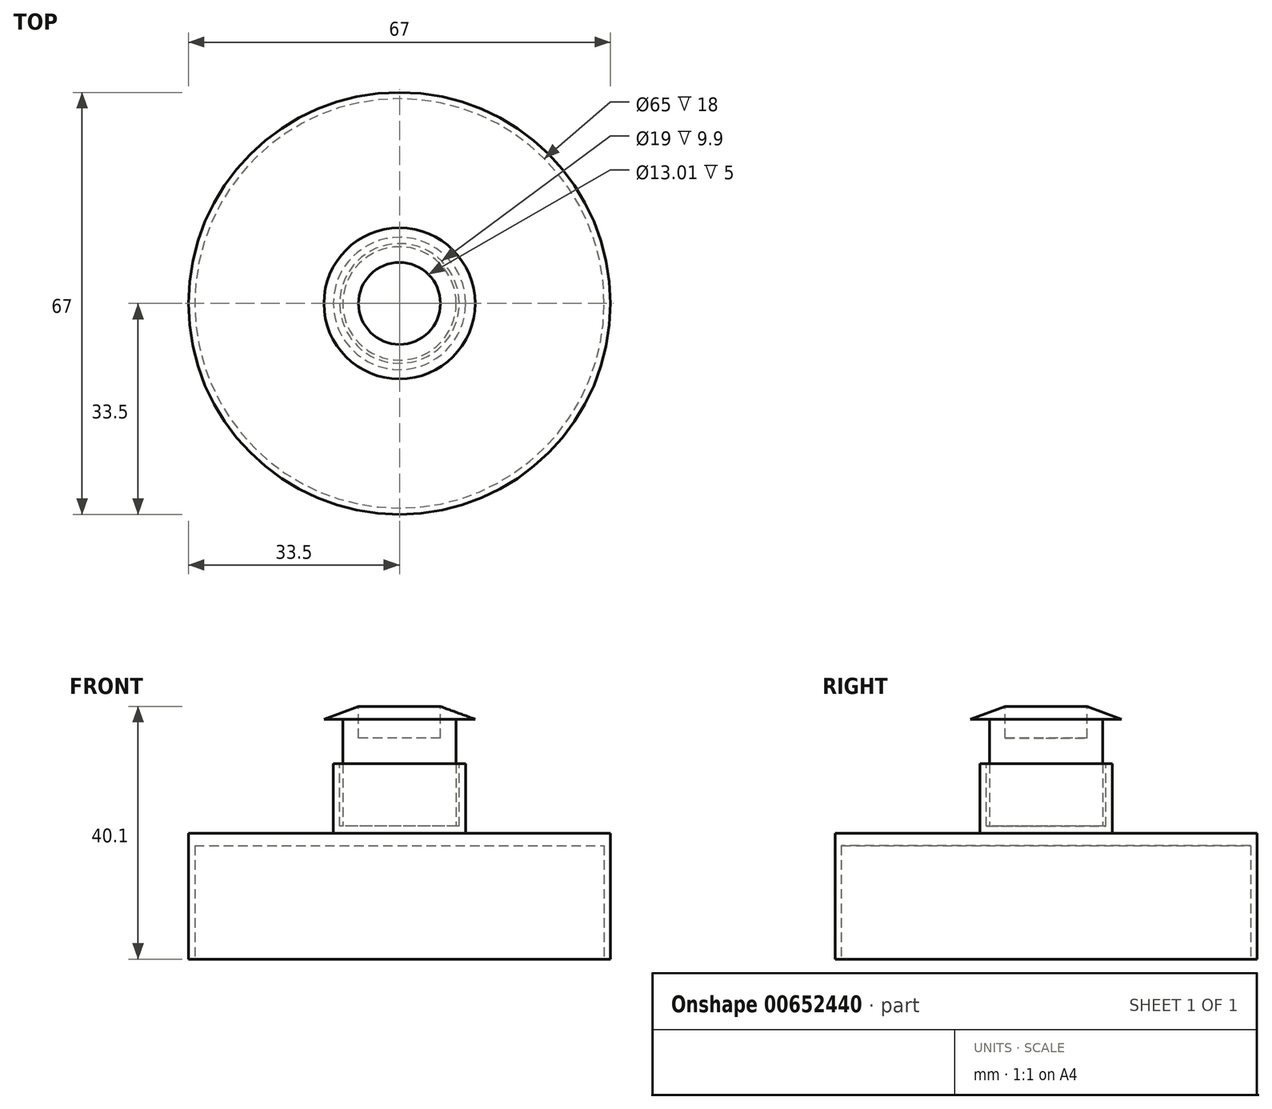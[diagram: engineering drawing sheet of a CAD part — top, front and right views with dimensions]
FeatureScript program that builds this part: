
annotation { "Feature Type Name" : "Feature", "Feature Type Description" : "" }
export const myFeature = defineFeature(function(context is Context, id is Id, definition is map)
    precondition{}
    {
        {
            var Q0;
            Q0=qCreatedBy(makeId("Top.planeOp"),FACE);
            var sketch = newSketch(context, id + "F0", { "sketchPlane" : qUnion([Q0])});
            skCircle(sketch, "E0", {"center": v(0, 0) * mm, "radius": 33.5 * mm});
            skSolve(sketch);
        }
        {
            var Q0;
            Q0 = qSketchRegion(id + "F0", true);
            var Q1;
            Q1 = qConstructionFilter(qBodyType(qCreatedBy(id + "F0" ,EDGE), BodyType.WIRE), ConstructionObject.NO);
            extrude(context, id + "F1", {"entities" : qUnion([Q0]), "surfaceEntities" : qUnion([Q1]), "depth" : 20 * mm, "offsetDistance" : 25 * mm});
        }
        {
            var Q0;
            Q0=makeQuery(id+"F1.opExtrude","CAP_FACE",FACE,{"disambiguationData":[OSD([sQuery(id+"F0.wireOp",EDGE,"E0")])],"isStart":true});
            var sketch = newSketch(context, id + "F2", { "sketchPlane" : qUnion([Q0])});
            skCircle(sketch, "E1", {"center": v(0, 0) * mm, "radius": 32.5 * mm});
            skSolve(sketch);
        }
        {
            var Q0;
            Q0=makeQuery(id+"F2.imprint","IMPRINT",FACE,{"disambiguationData":[TD([[makeQuery(id+"F2.imprint","IMPRINT",EDGE,{"derivedFrom":sQuery(id+"F2.wireOp",EDGE,"E1")}),1.0]])]});
            extrude(context, id + "F3", {"entities" : qUnion([Q0]), "operationType" : NewBodyOperationType.REMOVE, "oppositeDirection" : true, "depth" : 18 * mm, "offsetDistance" : 25 * mm});
        }
        {
            var Q0;
            Q0=makeQuery(id+"F1.opExtrude","CAP_FACE",FACE,{"disambiguationData":[OSD([sQuery(id+"F0.wireOp",EDGE,"E0")])],"isStart":false});
            var sketch = newSketch(context, id + "F4", { "sketchPlane" : qUnion([Q0])});
            skCircle(sketch, "E2", {"center": v(0, 0) * mm, "radius": 10.5 * mm});
            skSolve(sketch);
        }
        {
            var Q0;
            Q0=makeQuery(id+"F4.imprint","IMPRINT",FACE,{"disambiguationData":[TD([[makeQuery(id+"F4.imprint","IMPRINT",EDGE,{"derivedFrom":sQuery(id+"F4.wireOp",EDGE,"E2")}),1.0]])]});
            extrude(context, id + "F5", {"entities" : qUnion([Q0]), "operationType" : NewBodyOperationType.ADD, "depth" : 11 * mm, "offsetDistance" : 25 * mm});
        }
        {
            var Q0;
            Q0=makeQuery(id+"F5.opExtrude","CAP_FACE",FACE,{"disambiguationData":[OSD([sQuery(id+"F4.wireOp",EDGE,"E2")])],"isStart":false});
            var sketch = newSketch(context, id + "F6", { "sketchPlane" : qUnion([Q0])});
            skCircle(sketch, "E3", {"center": v(0, 0) * mm, "radius": 9.5 * mm});
            skSolve(sketch);
        }
        {
            var Q0;
            Q0=makeQuery(id+"F6.imprint","IMPRINT",FACE,{"disambiguationData":[TD([[makeQuery(id+"F6.imprint","IMPRINT",EDGE,{"derivedFrom":sQuery(id+"F6.wireOp",EDGE,"E3")}),1.0]])]});
            extrude(context, id + "F7", {"entities" : qUnion([Q0]), "operationType" : NewBodyOperationType.REMOVE, "oppositeDirection" : true, "depth" : 9.9 * mm, "offsetDistance" : 25 * mm});
        }
        {
            var Q0;
            Q0=makeQuery(id+"F7.boolean.opBoolean","COPY",FACE,{"derivedFrom":makeQuery(id+"F7.opExtrude","CAP_FACE",FACE,{"disambiguationData":[OSD([sQuery(id+"F6.wireOp",EDGE,"E3")])],"isStart":false})});
            var sketch = newSketch(context, id + "F8", { "sketchPlane" : qUnion([Q0])});
            skCircle(sketch, "E4", {"center": v(0, 0) * mm, "radius": 9 * mm});
            skSolve(sketch);
        }
        {
            var Q0;
            Q0=makeQuery(id+"F8.imprint","IMPRINT",FACE,{"disambiguationData":[TD([[makeQuery(id+"F8.imprint","IMPRINT",EDGE,{"derivedFrom":sQuery(id+"F8.wireOp",EDGE,"E4")}),1.0]])]});
            extrude(context, id + "F9", {"entities" : qUnion([Q0]), "operationType" : NewBodyOperationType.ADD, "depth" : 17 * mm, "offsetDistance" : 25 * mm});
        }
        {
            var Q0;
            Q0=makeQuery(id+"F9.opExtrude","CAP_FACE",FACE,{"disambiguationData":[OSD([sQuery(id+"F8.wireOp",EDGE,"E4")])],"isStart":false});
            var sketch = newSketch(context, id + "F10", { "sketchPlane" : qUnion([Q0])});
            skCircle(sketch, "E5", {"center": v(0, 0) * mm, "radius": 12 * mm});
            skSolve(sketch);
        }
        {
            var Q0;
            Q0 = qSketchRegion(id + "F10", true);
            extrude(context, id + "F11", {"entities" : qUnion([Q0]), "operationType" : NewBodyOperationType.ADD, "depth" : 2 * mm, "offsetDistance" : 25 * mm, "hasDraft" : true, "draftAngle" : 70 * degree, "draftPullDirection" : true});
        }
        {
            var Q0;
            Q0=makeQuery(id+"F11.opExtrude","CAP_FACE",FACE,{"disambiguationData":[OSD([sQuery(id+"F10.wireOp",EDGE,"E5")])],"isStart":false});
            extrude(context, id + "F12", {"entities" : qUnion([Q0]), "operationType" : NewBodyOperationType.REMOVE, "oppositeDirection" : true, "depth" : 5 * mm, "offsetDistance" : 25 * mm});
        }
    });
